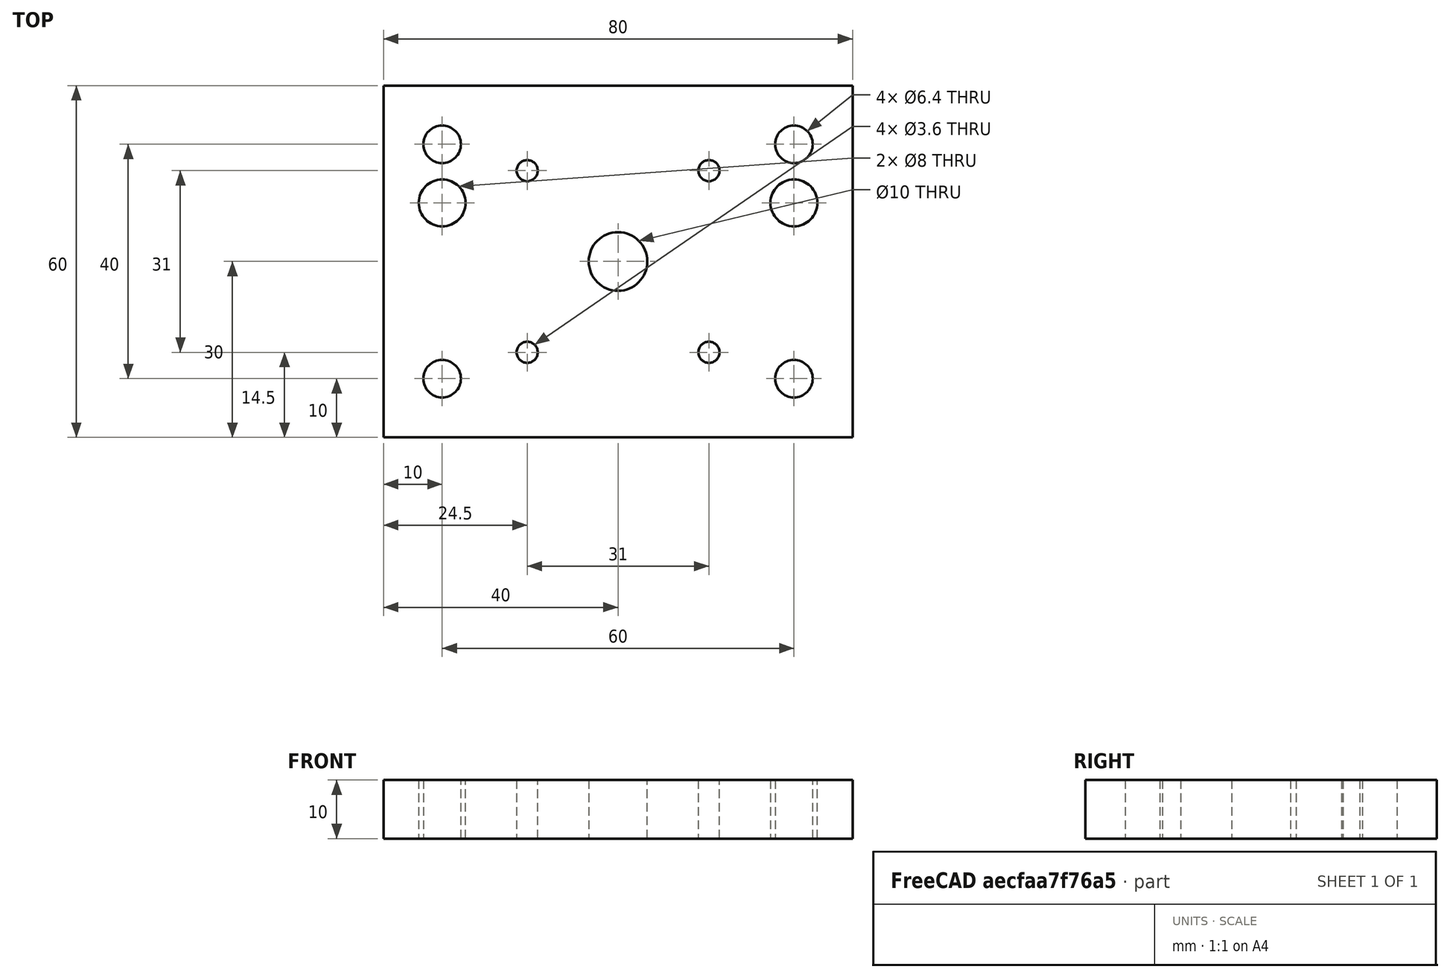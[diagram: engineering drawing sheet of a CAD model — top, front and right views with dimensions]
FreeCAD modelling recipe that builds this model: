
FCSTD DOCUMENT  (FreeCAD 0.18R16110 (Git))
Label: mountplate1b
License: All rights reserved
LicenseURL: http://en.wikipedia.org/wiki/All_rights_reserved
objects: Sketcher::SketchObject×1, PartDesign::Pad×1, PartDesign::Body×1
note: 4 computed .brp shape members not serialized (recipe doc carries the construction recipe); baked Part::Feature solids carry a one-line shape summary decoded from their .brp

FEATURE [Sketcher::SketchObject] Sketch
  MapMode = 5
  Support = -> [XY_Plane]
  sketch-geometry (15):
    g0: LineSegment StartX=0 StartY=60 StartZ=0 EndX=80 EndY=60 EndZ=0
    g1: LineSegment StartX=80 StartY=60 StartZ=0 EndX=80 EndY=0 EndZ=0
    g2: LineSegment StartX=80 StartY=0 StartZ=0 EndX=0 EndY=0 EndZ=0
    g3: LineSegment StartX=0 StartY=0 StartZ=0 EndX=0 EndY=60 EndZ=0
    g4: Circle CenterX=40 CenterY=30 CenterZ=0 NormalX=0 NormalY=0 NormalZ=1 AngleXU=0 Radius=5
    g5: Circle CenterX=55.5 CenterY=45.5 CenterZ=0 NormalX=0 NormalY=0 NormalZ=1 AngleXU=0 Radius=1.8
    g6: Circle CenterX=55.5 CenterY=14.5 CenterZ=0 NormalX=0 NormalY=0 NormalZ=1 AngleXU=0 Radius=1.8
    g7: Circle CenterX=24.5 CenterY=14.5 CenterZ=0 NormalX=0 NormalY=0 NormalZ=1 AngleXU=0 Radius=1.8
    g8: Circle CenterX=24.5 CenterY=45.5 CenterZ=0 NormalX=0 NormalY=0 NormalZ=1 AngleXU=0 Radius=1.8
    g9: Circle CenterX=10 CenterY=10 CenterZ=0 NormalX=0 NormalY=0 NormalZ=1 AngleXU=0 Radius=3.2
    g10: Circle CenterX=70 CenterY=10 CenterZ=0 NormalX=0 NormalY=0 NormalZ=1 AngleXU=0 Radius=3.2
    g11: Circle CenterX=70 CenterY=40 CenterZ=0 NormalX=0 NormalY=0 NormalZ=1 AngleXU=0 Radius=4
    g12: Circle CenterX=10 CenterY=40 CenterZ=0 NormalX=0 NormalY=0 NormalZ=1 AngleXU=0 Radius=4
    g13: Circle CenterX=10 CenterY=50 CenterZ=0 NormalX=0 NormalY=0 NormalZ=1 AngleXU=0 Radius=3.2
    g14: Circle CenterX=70 CenterY=50 CenterZ=0 NormalX=0 NormalY=0 NormalZ=1 AngleXU=0 Radius=3.2
  constraints (44):
    c: Coincident(g0,g1)
    c: Coincident(g1,g2)
    c: Coincident(g2,g3)
    c: Coincident(g3,g0)
    c: Horizontal(g0)
    c: Horizontal(g2)
    c: Vertical(g1)
    c: Vertical(g3)
    c: Coincident(g2,g-1)
    c: DistanceY(g3,g3) = 60
    c: DistanceX(g2,g2) = 80
    c: DistanceX(g2,g4) = 40
    c: DistanceY(g2,g4) = 30
    c: Radius(g4) = 5
    c: DistanceY(g4,g5) = 15.5
    c: DistanceX(g6,g5) = 0
    c: DistanceX(g4,g5) = 15.5
    c: DistanceY(g8,g5) = 0
    c: DistanceX(g8,g5) = 31
    c: DistanceX(g7,g8) = 0
    c: DistanceY(g6,g5) = 31
    c: DistanceY(g6,g7) = 0
    c: Radius(g8) = 1.8
    c: Equal(g8,g5)
    c: Equal(g8,g6)
    c: Equal(g8,g7)
    c: DistanceX(g2,g9) = 10
    c: DistanceY(g2,g9) = 10
    c: DistanceY(g9,g10) = 0
    c: DistanceX(g10,g1) = 10
    c: DistanceX(g12,g9) = 0
    c: DistanceY(g11,g12) = 0
    c: DistanceX(g11,g0) = 10
    c: DistanceY(g12,g0) = 20
    c: Radius(g9) = 3.2
    c: Equal(g9,g10)
    c: Radius(g12) = 4
    c: Equal(g12,g11)
    c: DistanceX(g11,g14) = 0
    c: DistanceX(g13,g12) = 0
    c: DistanceY(g13,g0) = 10
    c: DistanceY(g14,g0) = 10
    c: Radius(g14) = 3.2
    c: Radius(g13) = 3.2
FEATURE [PartDesign::Pad] Pad
  Length = 10
  Length2 = 100
  Profile = -> Sketch
  Type = 0
FEATURE [PartDesign::Body] Body
  Group = -> [Sketch,Pad]
  Origin = -> Origin
  Tip = -> Pad
